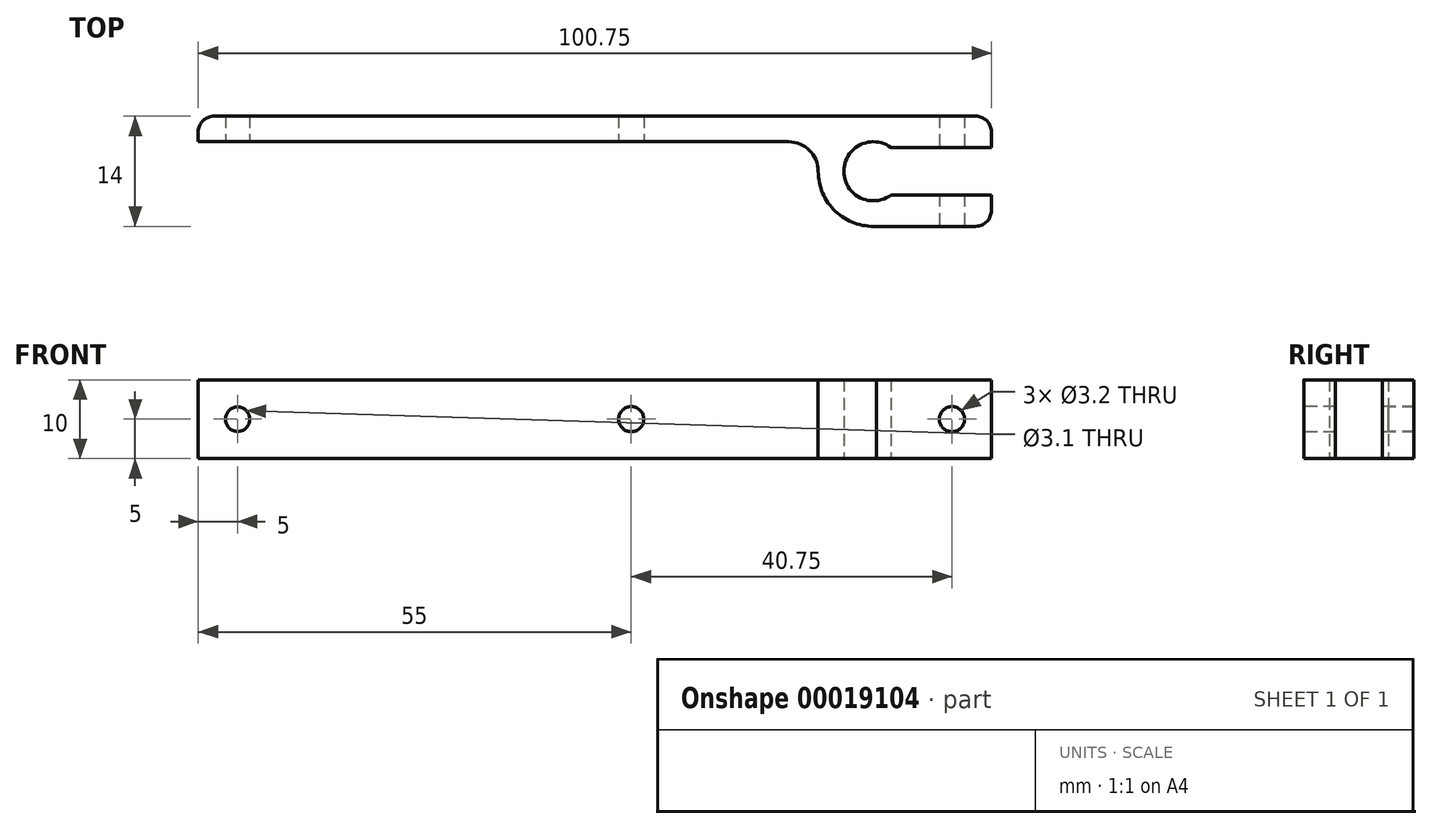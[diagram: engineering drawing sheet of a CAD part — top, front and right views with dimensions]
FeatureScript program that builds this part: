
annotation { "Feature Type Name" : "Feature", "Feature Type Description" : "" }
export const myFeature = defineFeature(function(context is Context, id is Id, definition is map)
    precondition{}
    {
        {
            var Q0;
            Q0=qCreatedBy(makeId("Top.planeOp"),FACE);
            var sketch = newSketch(context, id + "F0", { "sketchPlane" : qUnion([Q0])});
            skArc(sketch, "E0", {"start": v(-12.75, 8.6) * mm, "mid": v(-18.75, 5.59) * mm, "end": v(-12.73, 2.6) * mm});
            skArc(sketch, "E1", {"start": v(-22, 5.6) * mm, "mid": v(-19.8, 0.5) * mm, "end": v(-14.6, -1.4) * mm});
            skLineSegment(sketch, "E2.bottom", {"start": v(-15, 12.6) * mm, "end": v(-100.75, 12.6) * mm});
            skLineSegment(sketch, "E2.top", {"start": v(-25.75, 9.35) * mm, "end": v(-100.75, 9.35) * mm});
            skLineSegment(sketch, "E2.left", {"start": v(-15, 12.6) * mm, "end": v(-15, 9.35) * mm});
            skLineSegment(sketch, "E2.right", {"start": v(-100.75, 12.6) * mm, "end": v(-100.75, 9.35) * mm});
            skArc(sketch, "E3", {"start": v(-22, 5.6) * mm, "mid": v(-23.1, 8.25) * mm, "end": v(-25.75, 9.35) * mm});
            skLineSegment(sketch, "E4.bottom", {"start": v(-15, 12.6) * mm, "end": v(0, 12.6) * mm});
            skLineSegment(sketch, "E4.top", {"start": v(-15, -1.4) * mm, "end": v(0, -1.4) * mm});
            skLineSegment(sketch, "E4.right", {"start": v(0, 12.6) * mm, "end": v(0, 8.6) * mm});
            skLineSegment(sketch, "E5.bottom", {"start": v(-12.73, 2.6) * mm, "end": v(0, 2.6) * mm});
            skLineSegment(sketch, "E5.top", {"start": v(-12.75, 8.6) * mm, "end": v(0, 8.6) * mm});
            skLineSegment(sketch, "E6.trimOffspring", {"start": v(0, 2.6) * mm, "end": v(0, -1.4) * mm});
            skLineSegment(sketch, "E7.trimOffspring", {"start": v(-15, 1.85) * mm, "end": v(-15, -1.4) * mm});
            skSolve(sketch);
        }
        {
            var Q0;
            Q0=qSketchRegion(id+"F0",true);
            extrude(context, id + "F1", {"entities" : qUnion([Q0]), "depth" : 10 * mm});
        }
        {
            var Q0;
            Q0=makeQuery(id+"F1.opExtrude","SWEPT_FACE",FACE,{"disambiguationData":[OSD([sQuery(id+"F0.wireOp",EDGE,"E4.top")])]});
            var sketch = newSketch(context, id + "F2", { "sketchPlane" : qUnion([Q0])});
            skCircle(sketch, "E8", {"center": v(-5, 5) * mm, "radius": 1.6 * mm});
            skCircle(sketch, "E9", {"center": v(-45.75, 5) * mm, "radius": 1.6 * mm});
            skPoint(sketch, "E10", {"position": v(-100.75, 5) * mm});
            skCircle(sketch, "E11", {"center": v(-95.75, 5) * mm, "radius": 1.55 * mm});
            skSolve(sketch);
        }
        {
            var Q0;
            Q0=qSketchRegion(id+"F2",true);
            extrude(context, id + "F3", {"entities" : qUnion([Q0]), "operationType" : NewBodyOperationType.REMOVE, "endBound" : BoundingType.THROUGH_ALL, "oppositeDirection" : true, "depth" : 25 * mm});
        }
        {
            var Q0;
            Q0=makeQuery(id+"F1.opExtrude","SWEPT_EDGE",EDGE,{"disambiguationData":[OSD([sQuery(id+"F0.wireOp",EDGE,"E2.bottom"),sQuery(id+"F0.wireOp",EDGE,"E2.right")])]});
            var Q1;
            Q1=makeQuery(id+"F1.opExtrude","SWEPT_EDGE",EDGE,{"disambiguationData":[OSD([sQuery(id+"F0.wireOp",EDGE,"E4.top"),sQuery(id+"F0.wireOp",EDGE,"E6.trimOffspring")])]});
            var Q2;
            Q2=makeQuery(id+"F1.opExtrude","SWEPT_EDGE",EDGE,{"disambiguationData":[OSD([sQuery(id+"F0.wireOp",EDGE,"E4.bottom"),sQuery(id+"F0.wireOp",EDGE,"E4.right")])]});
            fillet(context, id + "F4", {"entities" : qUnion([Q0, Q1, Q2]), "radius" : 2 * mm, "tangentPropagation" : true, "allowEdgeOverflow" : false});
        }
    });
